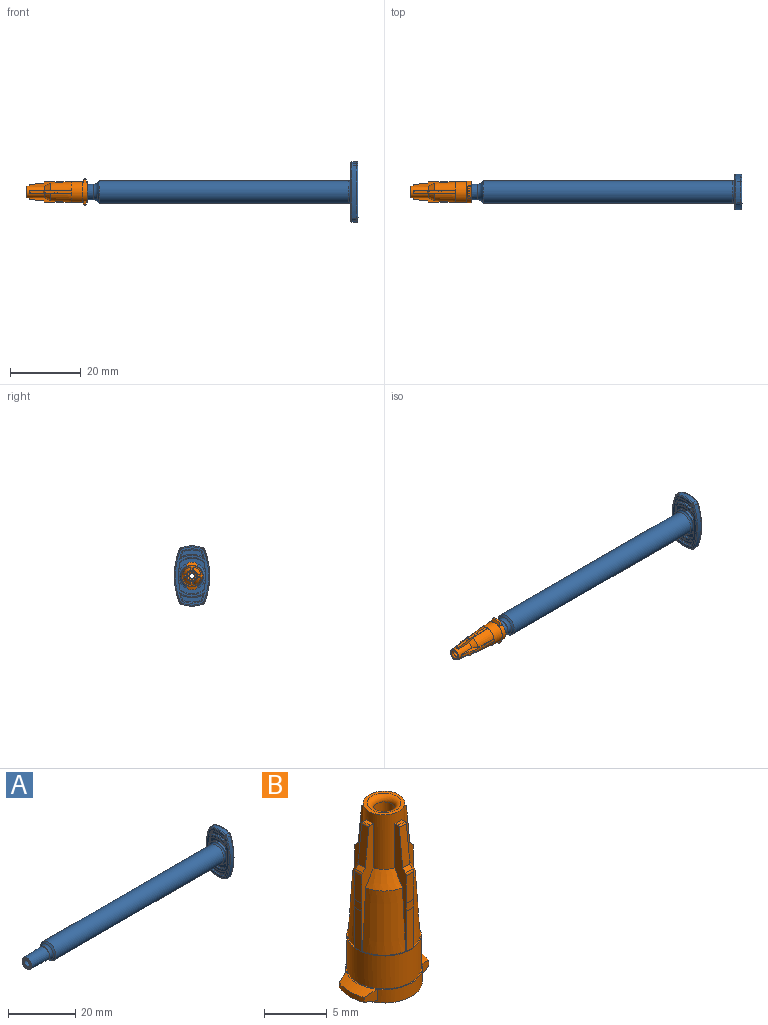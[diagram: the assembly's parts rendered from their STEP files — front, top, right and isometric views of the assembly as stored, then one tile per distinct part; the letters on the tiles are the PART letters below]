
ASSEMBLY  parts=2 mates=1
PART A: 74 faces, bbox 82.3x11x17.4 mm
  f0: plane 16.41x9.41mm, normal (-1,0,0), area 38.2mm2, adj f3,f34,f36,f39,f41,f48,f49,f50
  f1: cylinder r=8.5mm len=6.03mm, axis (1,0,0), area 8.6mm2, adj f25,f27,f49,f58
  f2: cylinder r=8.5mm len=6.03mm, axis (1,0,0), area 8.6mm2, adj f24,f26,f54,f61
  f3: torus R=3.8mm, axis (1,0,0), area 20.2mm2, adj f0,f4,f35,f38
  f4: cylinder r=3.2mm len=70.4mm, axis (1,0,0), area 1415.5mm2, adj f3,f5
  f5: cone r=3.2mm half-angle=46.7deg, axis (1,0,0), area 13.7mm2, adj f4,f6
  f6: torus R=3.69mm, axis (1,0,0), area 18mm2, adj f5,f7
  f7: cone r=2.19mm half-angle=0deg, axis (1,0,0), area 1.4mm2, adj f6,f8
  f8: cone r=1.97mm half-angle=1.7deg, axis (1,0,0), area 94.8mm2, adj f7,f9
  f9: torus R=1.72mm, axis (1,0,0), area 4.5mm2, adj f8,f10
  f10: plane 3.44x3.44mm, normal (-1,0,0), area 3.5mm2, adj f9,f11
  f11: cone r=1.35mm half-angle=15deg, axis (-1,0,0), area 1.7mm2, adj f10,f12
  f12: plane 2.6x2.6mm, normal (-1,0,0), area 1.8mm2, adj f11,f13
  f13: cone r=1.29mm half-angle=1.6deg, axis (1,0,0), area 62mm2, adj f12,f14
  f14: torus R=2.29mm, axis (1,0,0), area 6.9mm2, adj f13,f15
  f15: cone r=1.6mm half-angle=46.7deg, axis (1,0,0), area 12.9mm2, adj f14,f16
  f16: cylinder r=2.35mm len=67.56mm, axis (1,0,0), area 999.6mm2, adj f15,f17
  f17: cone r=2.36mm half-angle=0.8deg, axis (1,0,0), area 5.2mm2, adj f16,f18
  f18: cylinder r=2.36mm len=4.72mm, axis (1,0,0), area 19.3mm2, adj f17,f19
  f19: cone r=2.36mm half-angle=18.9deg, axis (-1,0,0), area 5.3mm2, adj f18,f20
  f20: cone r=2.93mm half-angle=14.8deg, axis (1,0,0), area 43.6mm2, adj f19,f21
  f21: plane 16.41x9.41mm, normal (1,0,0), area 105.7mm2, adj f20,f56,f57,f58,f59,f60,f61,f62
  f22: cylinder r=20mm len=14.76mm, axis (1,0,0), area 21.2mm2, adj f24,f25,f53,f62
  f23: cylinder r=20mm len=14.76mm, axis (1,0,0), area 21.2mm2, adj f26,f27,f50,f57
  f24: bspline ~2.2x0.58mm, area 1.2mm2, adj f2,f22,f55,f63
  f25: bspline ~2.2x0.58mm, area 1.2mm2, adj f1,f22,f51,f60
  f26: bspline ~2.2x0.58mm, area 1.2mm2, adj f2,f23,f52,f59
  f27: bspline ~2.2x0.58mm, area 1.2mm2, adj f1,f23,f48,f56
  f28: cylinder r=6.14mm len=6.12mm, axis (-1,0,0), area 1.9mm2, adj f29,f31,f32,f67
  f29: cylinder r=20mm len=1.56mm, axis (-1,0,0), area 0.5mm2, adj f28,f30,f32,f66
  f30: cylinder r=7.34mm len=5.12mm, axis (-1,0,0), area 1.6mm2, adj f29,f31,f32,f68
  f31: cylinder r=20mm len=1.56mm, axis (-1,0,0), area 0.5mm2, adj f28,f30,f32,f69
  f32: plane 6.12x2.02mm, normal (-1,0,0), area 7mm2, adj f28,f29,f30,f31
  f33: cylinder r=4.98mm len=6.91mm, axis (-1,0,0), area 2.3mm2, adj f34,f36,f37,f65
  f34: cylinder r=20mm len=3.64mm, axis (-1,0,0), area 2mm2, adj f0,f33,f35,f37,f65
  f35: cylinder r=3.8mm len=7.55mm, axis (-1,0,0), area 6.6mm2, adj f3,f34,f36,f37
  f36: cylinder r=20mm len=3.64mm, axis (-1,0,0), area 2mm2, adj f0,f33,f35,f37,f65
  f37: plane 7.55x4.55mm, normal (-1,0,0), area 10.3mm2, adj f33,f34,f35,f36
  f38: cylinder r=3.8mm len=7.55mm, axis (-1,0,0), area 6.6mm2, adj f3,f39,f41,f42
  f39: cylinder r=20mm len=3.64mm, axis (-1,0,0), area 2mm2, adj f0,f38,f40,f42,f64
  f40: cylinder r=4.98mm len=6.91mm, axis (-1,0,0), area 2.3mm2, adj f39,f41,f42,f64
  f41: cylinder r=20mm len=3.64mm, axis (-1,0,0), area 2mm2, adj f0,f38,f40,f42,f64
  f42: plane 7.55x4.55mm, normal (-1,0,0), area 10.3mm2, adj f38,f39,f40,f41
  f43: cylinder r=7.34mm len=5.12mm, axis (-1,0,0), area 1.6mm2, adj f44,f46,f47,f71
  f44: cylinder r=20mm len=1.56mm, axis (-1,0,0), area 0.5mm2, adj f43,f45,f47,f70
  f45: cylinder r=6.14mm len=6.12mm, axis (-1,0,0), area 1.9mm2, adj f44,f46,f47,f72
  f46: cylinder r=20mm len=1.56mm, axis (-1,0,0), area 0.5mm2, adj f43,f45,f47,f73
  f47: plane 6.12x2.02mm, normal (-1,0,0), area 7mm2, adj f43,f44,f45,f46
  f48: bspline ~0.68x0.68mm, area 0.4mm2, adj f0,f27,f49,f50
  f49: bspline ~6.03x1.02mm, area 3mm2, adj f0,f1,f48,f51
  f50: bspline ~14.76x2.17mm, area 7.3mm2, adj f0,f23,f48,f52
  f51: bspline ~0.68x0.68mm, area 0.4mm2, adj f0,f25,f49,f53
  f52: bspline ~0.68x0.68mm, area 0.4mm2, adj f0,f26,f50,f54
  f53: bspline ~14.76x2.17mm, area 7.3mm2, adj f0,f22,f51,f55
  f54: bspline ~6.03x1.02mm, area 3mm2, adj f0,f2,f52,f55
  f55: bspline ~0.68x0.68mm, area 0.4mm2, adj f0,f24,f53,f54
  f56: bspline ~0.68x0.68mm, area 0.4mm2, adj f21,f27,f57,f58
  f57: bspline ~14.76x2.17mm, area 7.3mm2, adj f21,f23,f56,f59
  f58: bspline ~6.03x1.02mm, area 3mm2, adj f1,f21,f56,f60
  f59: bspline ~0.68x0.68mm, area 0.4mm2, adj f21,f26,f57,f61
  f60: bspline ~0.68x0.68mm, area 0.4mm2, adj f21,f25,f58,f62
  f61: bspline ~6.03x1.02mm, area 3mm2, adj f2,f21,f59,f63
  f62: bspline ~14.76x2.17mm, area 7.3mm2, adj f21,f22,f60,f63
  f63: bspline ~0.68x0.68mm, area 0.4mm2, adj f21,f24,f61,f62
  f64: bspline ~7.89x2.13mm, area 3.6mm2, adj f0,f39,f40,f41
  f65: bspline ~7.89x2.13mm, area 3.6mm2, adj f0,f33,f34,f36
  f66: bspline ~2.73x1.09mm, area 1mm2, adj f0,f29,f67,f68
  f67: bspline ~7.45x1.5mm, area 3.5mm2, adj f0,f28,f66,f69
  f68: bspline ~5.59x0.81mm, area 2.7mm2, adj f0,f30,f66,f69
  f69: bspline ~2.73x1.09mm, area 1mm2, adj f0,f31,f67,f68
  f70: bspline ~2.73x1.09mm, area 1mm2, adj f0,f44,f71,f72
  f71: bspline ~5.59x0.81mm, area 2.7mm2, adj f0,f43,f70,f73
  f72: bspline ~7.45x1.5mm, area 3.5mm2, adj f0,f45,f70,f73
  f73: bspline ~2.73x1.09mm, area 1mm2, adj f0,f46,f71,f72
PART B: 78 faces, bbox 7.9x6.2x17.4 mm
  f0: plane 5.9x5.9mm, normal (0,0,1), area 1.6mm2, adj f1,f3,f5,f14,f15,f44,f46,f47
  f1: cone r=2.5mm half-angle=3.3deg, axis (0,0,-1), area 20.4mm2, adj f0,f2,f47,f77
  f2: cone r=1.65mm half-angle=29.5deg, axis (0,0,-1), area 4.2mm2, adj f1,f17,f47,f77
  f3: cone r=2.5mm half-angle=3.3deg, axis (0,0,-1), area 20.4mm2, adj f0,f4,f46,f67
  f4: cone r=1.65mm half-angle=29.5deg, axis (0,0,-1), area 4.2mm2, adj f3,f17,f46,f67
  f5: cone r=2.5mm half-angle=3.3deg, axis (0,0,-1), area 20.4mm2, adj f0,f6,f57,f76
  f6: cone r=1.65mm half-angle=29.5deg, axis (0,0,-1), area 4.2mm2, adj f5,f17,f57,f76
  f7: cylinder r=3.89mm len=2.81mm, axis (0,0,1), area 1.4mm2, adj f10,f12,f35,f37
  f8: cylinder r=3.89mm len=2.81mm, axis (0,0,1), area 1.4mm2, adj f9,f11,f34,f36
  f9: cone r=3.05mm half-angle=75deg, axis (0,0,1), area 2.9mm2, adj f8,f33,f34,f36
  f10: cone r=3.05mm half-angle=75deg, axis (0,0,1), area 2.9mm2, adj f7,f33,f35,f37
  f11: cone r=3.89mm half-angle=65deg, axis (0,0,-1), area 3.1mm2, adj f8,f13,f34,f36
  f12: cone r=3.89mm half-angle=65deg, axis (0,0,-1), area 3.1mm2, adj f7,f13,f35,f37
  f13: cone r=2.95mm half-angle=89.9deg, axis (0,0,-1), area 1.9mm2, adj f11,f12,f14,f33
  f14: cylinder r=2.95mm len=5.9mm, axis (0,0,1), area 59.3mm2, adj f0,f13
  f15: cone r=2.5mm half-angle=3.3deg, axis (0,0,-1), area 20.4mm2, adj f0,f16,f56,f66
  f16: cone r=1.65mm half-angle=29.5deg, axis (0,0,-1), area 4.2mm2, adj f15,f17,f56,f66
  f17: cylinder r=1.65mm len=5.3mm, axis (0,0,1), area 41mm2, adj f2,f4,f6,f16,f18,f43,f46,f47
  f18: plane 3.3x3.3mm, normal (0,0,1), area 2.8mm2, adj f17,f19
  f19: torus R=1.35mm, axis (0,0,1), area 5.1mm2, adj f18,f20
  f20: cylinder r=0.85mm len=5.8mm, axis (0,0,1), area 31mm2, adj f19,f21
  f21: plane 1.7x1.7mm, normal (0,0,1), area 0.6mm2, adj f20,f22
  f22: cylinder r=0.72mm len=1.45mm, axis (0,0,1), area 3.6mm2, adj f21,f23
  f23: plane 2.7x2.7mm, normal (0,0,-1), area 4.1mm2, adj f22,f24
  f24: cylinder r=1.35mm len=2.7mm, axis (0,0,1), area 2.5mm2, adj f23,f25
  f25: torus R=1.33mm, axis (0,0,1), area 7.7mm2, adj f24,f26
  f26: cone r=1.85mm half-angle=1.7deg, axis (0,0,-1), area 7.3mm2, adj f25,f27
  f27: torus R=1.55mm, axis (0,0,1), area 2.6mm2, adj f26,f28
  f28: torus R=2.25mm, axis (0,0,1), area 10mm2, adj f27,f29
  f29: torus R=1.59mm, axis (0,0,1), area 2.6mm2, adj f28,f30
  f30: cone r=1.89mm half-angle=1.7deg, axis (0,0,-1), area 99.7mm2, adj f29,f31
  f31: torus R=2.38mm, axis (0,0,1), area 5.4mm2, adj f30,f32
  f32: plane 6.1x6.1mm, normal (0,0,-1), area 11.5mm2, adj f31,f33
  f33: cylinder r=3.05mm len=6.1mm, axis (0,0,1), area 16.7mm2, adj f9,f10,f13,f32,f34,f35,f36,f37
  f34: plane 1.25x1.22mm, normal (-0.29,0.96,0), area 0.9mm2, adj f8,f9,f11,f33
  f35: plane 1.25x1.22mm, normal (0.29,0.96,0), area 0.9mm2, adj f7,f10,f12,f33
  f36: plane 1.25x1.22mm, normal (-0.29,-0.96,0), area 0.9mm2, adj f8,f9,f11,f33
  f37: plane 1.25x1.22mm, normal (0.29,-0.96,0), area 0.9mm2, adj f7,f10,f12,f33
  f38: plane 2.7x0.8mm, normal (0,1,-0.01), area 2.2mm2, adj f39,f45,f46,f47
  f39: cylinder r=0.3mm len=0.8mm, axis (-1,0,0), area 0.2mm2, adj f38,f40,f46,f47
  f40: plane 0.8x0.32mm, normal (0,0.71,0.71), area 0.4mm2, adj f39,f41,f46,f47
  f41: plane 3.76x0.8mm, normal (0,0.99,0.1), area 3mm2, adj f40,f42,f46,f47
  f42: cylinder r=0.15mm len=0.8mm, axis (-1,0,0), area 0.2mm2, adj f41,f43,f46,f47
  f43: plane 0.8x0.36mm, normal (0,0,1), area 0.3mm2, adj f17,f42,f46,f47
  f44: plane 3.9x0.8mm, normal (0,1,0.01), area 3.1mm2, adj f0,f45,f46,f47
  f45: plane 0.8x0.77mm, normal (0,1,0), area 0.6mm2, adj f38,f44,f46,f47
  f46: plane 11.84x1.35mm, normal (1,0,0), area 5.9mm2, adj f0,f3,f4,f17,f38,f39,f40,f41
  f47: plane 11.84x1.35mm, normal (-1,0,0), area 5.9mm2, adj f0,f1,f2,f17,f38,f39,f40,f41
  f48: plane 0.8x0.36mm, normal (0,0,1), area 0.3mm2, adj f17,f49,f56,f57
  f49: cylinder r=0.15mm len=0.8mm, axis (-1,0,0), area 0.2mm2, adj f48,f50,f56,f57
  f50: plane 3.76x0.8mm, normal (0,-0.99,0.1), area 3mm2, adj f49,f51,f56,f57
  f51: plane 0.8x0.32mm, normal (0,-0.71,0.71), area 0.4mm2, adj f50,f52,f56,f57
  f52: cylinder r=0.3mm len=0.8mm, axis (-1,0,0), area 0.2mm2, adj f51,f53,f56,f57
  f53: plane 2.7x0.8mm, normal (0,-1,-0.01), area 2.2mm2, adj f52,f54,f56,f57
  f54: plane 0.8x0.77mm, normal (0,-1,0), area 0.6mm2, adj f53,f55,f56,f57
  f55: plane 3.9x0.8mm, normal (0,-1,0.01), area 3.1mm2, adj f0,f54,f56,f57
  f56: plane 11.84x1.35mm, normal (1,0,0), area 5.9mm2, adj f0,f15,f16,f17,f48,f49,f50,f51
  f57: plane 11.84x1.35mm, normal (-1,0,0), area 5.9mm2, adj f0,f5,f6,f17,f48,f49,f50,f51
  f58: plane 2.7x0.8mm, normal (1,0,-0.01), area 2.2mm2, adj f59,f65,f66,f67
  f59: cylinder r=0.3mm len=0.8mm, axis (0,1,0), area 0.2mm2, adj f58,f60,f66,f67
  f60: plane 0.8x0.32mm, normal (0.71,0,0.71), area 0.4mm2, adj f59,f61,f66,f67
  f61: plane 3.76x0.8mm, normal (0.99,0,0.1), area 3mm2, adj f60,f62,f66,f67
  f62: cylinder r=0.15mm len=0.8mm, axis (0,1,0), area 0.2mm2, adj f61,f63,f66,f67
  f63: plane 0.8x0.36mm, normal (0,0,1), area 0.3mm2, adj f17,f62,f66,f67
  f64: plane 3.9x0.8mm, normal (1,0,0.01), area 3.1mm2, adj f0,f65,f66,f67
  f65: plane 0.8x0.77mm, normal (1,0,0), area 0.6mm2, adj f58,f64,f66,f67
  f66: plane 11.84x1.35mm, normal (0,-1,0), area 5.9mm2, adj f0,f15,f16,f17,f58,f59,f60,f61
  f67: plane 11.84x1.35mm, normal (0,1,0), area 5.9mm2, adj f0,f3,f4,f17,f58,f59,f60,f61
  f68: plane 0.8x0.36mm, normal (0,0,1), area 0.3mm2, adj f17,f69,f76,f77
  f69: cylinder r=0.15mm len=0.8mm, axis (0,1,0), area 0.2mm2, adj f68,f70,f76,f77
  f70: plane 3.76x0.8mm, normal (-0.99,0,0.1), area 3mm2, adj f69,f71,f76,f77
  f71: plane 0.8x0.32mm, normal (-0.71,0,0.71), area 0.4mm2, adj f70,f72,f76,f77
  f72: cylinder r=0.3mm len=0.8mm, axis (0,1,0), area 0.2mm2, adj f71,f73,f76,f77
  f73: plane 2.7x0.8mm, normal (-1,0,-0.01), area 2.2mm2, adj f72,f74,f76,f77
  f74: plane 0.8x0.77mm, normal (-1,0,0), area 0.6mm2, adj f73,f75,f76,f77
  f75: plane 3.9x0.8mm, normal (-1,0,0.01), area 3.1mm2, adj f0,f74,f76,f77
  f76: plane 11.84x1.35mm, normal (0,-1,0), area 5.9mm2, adj f0,f5,f6,f17,f68,f69,f70,f71
  f77: plane 11.84x1.35mm, normal (0,1,0), area 5.9mm2, adj f0,f1,f2,f17,f68,f69,f70,f71
PLACE A rot(axis=(-0.31,-0.39,0.86),0deg) t=(-3.26,13.25,-14.3)mm
PLACE B rot(axis=(0,-1,0),90deg) t=(-79.56,13.25,-14.3)mm
MATE slider B.f1 <-> A.f11  axis (1,0,0) through (-79.56,13.25,-14.3)mm
